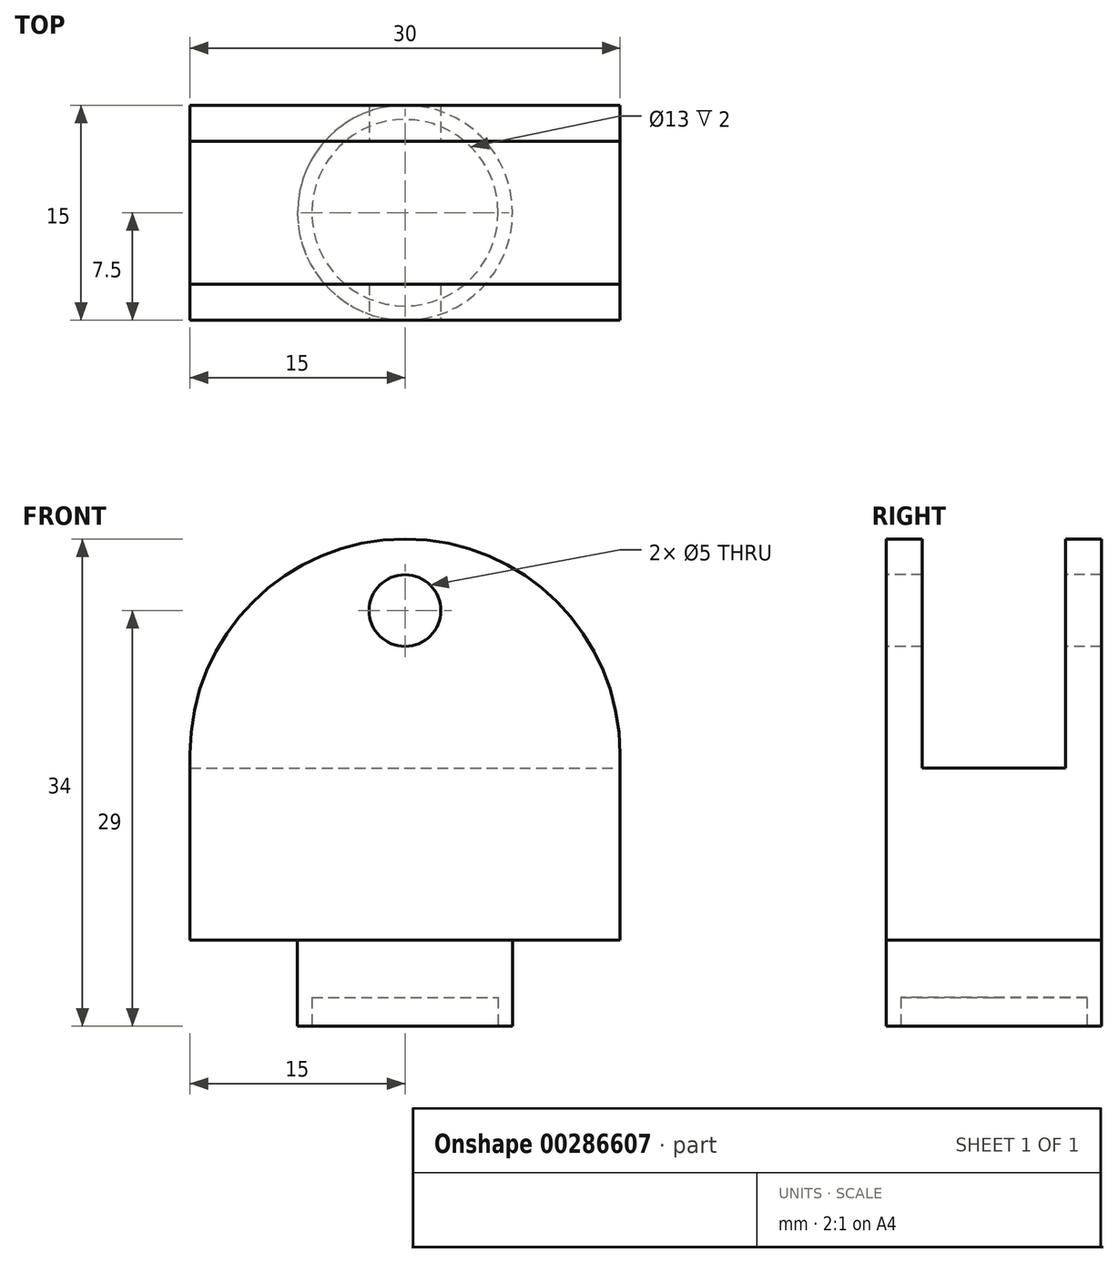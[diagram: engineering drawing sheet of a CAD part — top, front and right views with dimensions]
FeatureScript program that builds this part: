
annotation { "Feature Type Name" : "Feature", "Feature Type Description" : "" }
export const myFeature = defineFeature(function(context is Context, id is Id, definition is map)
    precondition{}
    {
        {
            var Q0;
            Q0=qCreatedBy(makeId("Front.planeOp"),FACE);
            var sketch = newSketch(context, id + "F0", { "sketchPlane" : qUnion([Q0])});
            skLineSegment(sketch, "E0.bottom", {"start": v(-15, 6) * mm, "end": v(15, 6) * mm});
            skLineSegment(sketch, "E0.top", {"start": v(-15, -6) * mm, "end": v(15, -6) * mm});
            skLineSegment(sketch, "E0.left", {"start": v(-15, 6) * mm, "end": v(-15, -6) * mm});
            skLineSegment(sketch, "E0.right", {"start": v(15, 6) * mm, "end": v(15, -6) * mm});
            skPoint(sketch, "E0.middle", {"position": v(0, 0) * mm});
            skArc(sketch, "E1", {"start": v(15, 6) * mm, "mid": v(0, 21) * mm, "end": v(-15, 6) * mm});
            skSolve(sketch);
        }
        {
            var Q0;
            Q0=makeQuery(id+"F0.imprint","IMPRINT",FACE,{"disambiguationData":[TD([[makeQuery(id+"F0.imprint","IMPRINT",EDGE,{"derivedFrom":sQuery(id+"F0.wireOp",EDGE,"E0.bottom")}),-1.0]])]});
            extrude(context, id + "F1", {"entities" : qUnion([Q0]), "depth" : 15 * mm});
        }
        {
            var Q0;
            Q0=makeQuery(id+"F1.opExtrude","CAP_FACE",FACE,{"disambiguationData":[OSD([sQuery(id+"F0.wireOp",EDGE,"E0.bottom"),sQuery(id+"F0.wireOp",EDGE,"E0.top"),sQuery(id+"F0.wireOp",EDGE,"E0.left"),sQuery(id+"F0.wireOp",EDGE,"E0.right")])],"isStart":true});
            var sketch = newSketch(context, id + "F2", { "sketchPlane" : qUnion([Q0])});
            skLineSegment(sketch, "E2.bottom", {"start": v(-15, 6) * mm, "end": v(15, 6) * mm});
            skLineSegment(sketch, "E2.top", {"start": v(-15, 7) * mm, "end": v(15, 7) * mm});
            skLineSegment(sketch, "E2.left", {"start": v(-15, 6) * mm, "end": v(-15, 7) * mm});
            skLineSegment(sketch, "E2.right", {"start": v(15, 6) * mm, "end": v(15, 7) * mm});
            skArc(sketch, "E3", {"start": v(15, 7) * mm, "mid": v(0, 22) * mm, "end": v(-15, 7) * mm});
            skSolve(sketch);
        }
        {
            var Q0;
            Q0=makeQuery(id+"F2.imprint","IMPRINT",FACE,{"disambiguationData":[TD([[makeQuery(id+"F2.imprint","IMPRINT",EDGE,{"derivedFrom":sQuery(id+"F2.wireOp",EDGE,"NGfHuBH4-hP9g-t1F1-idxl-9O1YGswrCCW4")}),1.0]])]});
            var Q1;
            Q1=makeQuery(id+"F2.imprint","IMPRINT",FACE,{"disambiguationData":[TD([[makeQuery(id+"F2.imprint","IMPRINT",EDGE,{"derivedFrom":sQuery(id+"F2.wireOp",EDGE,"E2.bottom")}),-1.0]])]});
            var Q2;
            Q2=makeQuery(id+"F2.imprint","IMPRINT",FACE,{"disambiguationData":[TD([[makeQuery(id+"F2.imprint","IMPRINT",EDGE,{"derivedFrom":sQuery(id+"F2.wireOp",EDGE,"E2.top")}),1.0]])]});
            extrude(context, id + "F3", {"entities" : qUnion([Q0, Q1, Q2]), "operationType" : NewBodyOperationType.ADD, "oppositeDirection" : true, "depth" : 2.5 * mm});
        }
        {
            var Q0;
            Q0=makeQuery(id+"F1.opExtrude","CAP_FACE",FACE,{"disambiguationData":[OSD([sQuery(id+"F0.wireOp",EDGE,"E0.bottom"),sQuery(id+"F0.wireOp",EDGE,"E0.top"),sQuery(id+"F0.wireOp",EDGE,"E0.left"),sQuery(id+"F0.wireOp",EDGE,"E0.right")])],"isStart":false});
            var sketch = newSketch(context, id + "F4", { "sketchPlane" : qUnion([Q0])});
            skLineSegment(sketch, "E4.bottom", {"start": v(-15, 6) * mm, "end": v(15, 6) * mm});
            skLineSegment(sketch, "E4.top", {"start": v(-15, 7) * mm, "end": v(15, 7) * mm});
            skLineSegment(sketch, "E4.left", {"start": v(-15, 6) * mm, "end": v(-15, 7) * mm});
            skLineSegment(sketch, "E4.right", {"start": v(15, 6) * mm, "end": v(15, 7) * mm});
            skArc(sketch, "E5", {"start": v(15, 7) * mm, "mid": v(0, 22) * mm, "end": v(-15, 7) * mm});
            skSolve(sketch);
        }
        {
            var Q0;
            Q0 = qSketchRegion(id + "F4", true);
            var Q1;
            Q1=makeQuery(id+"F4.imprint","IMPRINT",FACE,{"disambiguationData":[TD([[makeQuery(id+"F4.imprint","IMPRINT",EDGE,{"derivedFrom":sQuery(id+"F4.wireOp",EDGE,"dLSNcV41-Splj-C6K3-8Bfd-GCTFyQodpQ4Z")}),1.0]])]});
            extrude(context, id + "F5", {"entities" : qUnion([Q0, Q1]), "operationType" : NewBodyOperationType.ADD, "oppositeDirection" : true, "depth" : 2.5 * mm});
        }
        {
            var Q0;
            {var subQ0=sQuery(id+"F0.wireOp",EDGE,"E0.bottom");Q0=makeQuery(id+"F5.boolean.opBoolean","MERGE",FACE,{"derivedFrom":[makeQuery(id+"F1.opExtrude","CAP_FACE",FACE,{"disambiguationData":[OSD([subQ0,sQuery(id+"F0.wireOp",EDGE,"E0.top"),sQuery(id+"F0.wireOp",EDGE,"E0.left"),sQuery(id+"F0.wireOp",EDGE,"E0.right")])],"isStart":false}),makeQuery(id+"F5.opExtrude","CAP_FACE",FACE,{"disambiguationData":[OSD([subQ0,sQuery(id+"F4.wireOp",EDGE,"dLSNcV41-Splj-C6K3-8Bfd-GCTFyQodpQ4Z")])],"isStart":true})]});}
            var sketch = newSketch(context, id + "F6", { "sketchPlane" : qUnion([Q0])});
            skCircle(sketch, "E6", {"center": v(0, 17) * mm, "radius": 2.5 * mm});
            skPoint(sketch, "E6.centerSnap0", {"position": v(0, 20.75) * mm});
            skSolve(sketch);
        }
        {
            var Q0;
            Q0=makeQuery(id+"F6.imprint","IMPRINT",FACE,{"disambiguationData":[TD([[makeQuery(id+"F6.imprint","IMPRINT",EDGE,{"derivedFrom":sQuery(id+"F6.wireOp",EDGE,"E6")}),1.0]])]});
            extrude(context, id + "F7", {"entities" : qUnion([Q0]), "operationType" : NewBodyOperationType.REMOVE, "endBound" : BoundingType.THROUGH_ALL, "oppositeDirection" : true, "depth" : 25 * mm});
        }
        {
            var Q0;
            Q0=makeQuery(id+"F1.opExtrude","SWEPT_FACE",FACE,{"disambiguationData":[OSD([sQuery(id+"F0.wireOp",EDGE,"E0.top")])]});
            var sketch = newSketch(context, id + "F8", { "sketchPlane" : qUnion([Q0])});
            skCircle(sketch, "E7", {"center": v(0, 7.5) * mm, "radius": 7.5 * mm});
            skPoint(sketch, "E7.centerSnap0", {"position": v(-15, 7.5) * mm});
            skSolve(sketch);
        }
        {
            var Q0;
            {var subQ0=sQuery(id+"F8.wireOp",EDGE,"E7");var subQ1=sQuery(id+"F0.wireOp",EDGE,"E0.top");var subQ2=makeQuery(id+"F8.imprint","INTERSECT",VERTEX,{"derivedFrom":[makeQuery(id+"F1.opExtrude","CAP_EDGE",EDGE,{"disambiguationData":[OSD([subQ1])],"isStart":true}),subQ0]});Q0=makeQuery(id+"F8.imprint","IMPRINT",FACE,{"disambiguationData":[TD([[makeQuery(id+"F8.imprint","IMPRINT",EDGE,{"disambiguationData":[TD([[subQ2,1.0]])],"derivedFrom":subQ0}),1.0]])]});}
            extrude(context, id + "F9", {"entities" : qUnion([Q0]), "operationType" : NewBodyOperationType.ADD, "depth" : 6 * mm});
        }
        {
            var Q0;
            Q0=makeQuery(id+"F9.opExtrude","CAP_FACE",FACE,{"disambiguationData":[OSD([sQuery(id+"F8.wireOp",EDGE,"E7")])],"isStart":false});
            var sketch = newSketch(context, id + "F10", { "sketchPlane" : qUnion([Q0])});
            skCircle(sketch, "E8", {"center": v(0, 7.5) * mm, "radius": 6.5 * mm});
            skSolve(sketch);
        }
        {
            var Q0;
            Q0=makeQuery(id+"F10.imprint","IMPRINT",FACE,{"disambiguationData":[TD([[makeQuery(id+"F10.imprint","IMPRINT",EDGE,{"derivedFrom":sQuery(id+"F10.wireOp",EDGE,"E8")}),1.0]])]});
            var Q1;
            {var subQ0=sQuery(id+"F0.wireOp",EDGE,"E0.right");var subQ1=sQuery(id+"F0.wireOp",EDGE,"E0.top");var subQ2=makeQuery(id+"F1.opExtrude","SWEPT_FACE",FACE,{"disambiguationData":[OSD([subQ1])]});Q1=makeQuery(id+"F9.boolean.opBoolean","SPLIT",FACE,{"disambiguationData":[TD([makeQuery(id+"F1.opExtrude","SWEPT_FACE",FACE,{"disambiguationData":[OSD([subQ0])]})])],"derivedFrom":subQ2});}
            extrude(context, id + "F11", {"entities" : qUnion([Q0]), "operationType" : NewBodyOperationType.REMOVE, "oppositeDirection" : true, "endBoundEntityFace" : qUnion([Q1]), "depth" : 2 * mm});
        }
    });
